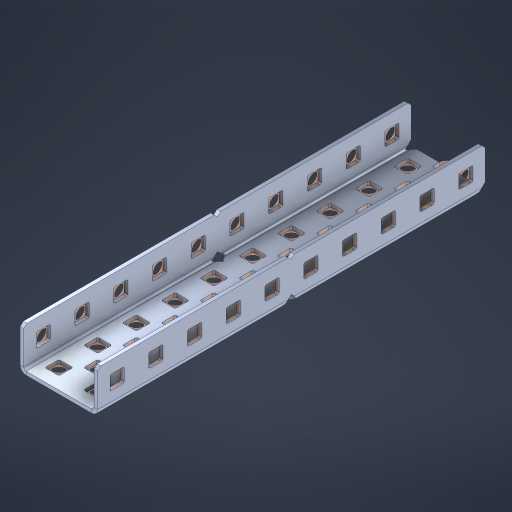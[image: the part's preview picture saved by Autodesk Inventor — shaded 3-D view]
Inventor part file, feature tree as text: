
AUTODESK INVENTOR PART (.ipt)
format: ipt  version: 2023 (Build 270158000, 158)  size: 927,744 bytes
history: native  units: in
note: dims shown in document units (in); Inventor stores cm internally (conversion verified against a paired STEP export)
features: other x57, extrude x48, sheet_metal_op x11, sketch x10, pattern_linear x2, mirror x1, chamfer x1
ambient origin geometry x8: Origin, YZ Plane, XZ Plane, XY Plane, X Axis, Y Axis, Z Axis, Center Point
bodies: Solid1 (feature_tree), Body (feature_tree)
feature tree (130):
  sheet_metal_op  "Flanges"
  other  "Flange Pattern Plane"
  other  "Flange Pattern Sketch"
  sheet_metal_op  "Flange Pattern"
  sheet_metal_op  "Body Pattern"
  pattern_linear  "Center Pattern"  Spacing1=0.0469in  [1 undecoded]
  other  "Arc Length"
  mirror  "Notch Mirror"
  pattern_linear  "Notch Pattern"  Spacing1=0.182in  [1 undecoded]
  chamfer  "End Chamfer"
  extrude  "Half Cut"  Depth=0.02in
  sketch  "Sketch1"  dims[d0=1.0in]
  other  "Plate1"
  sketch  "Sketch2"  dims[d1=5.0in]
  other  "Plate2"
  sheet_metal_op  "Bend1"
  sheet_metal_op  "Corner1"
  sketch  "Sketch3"  dims[d2=0.0469in]
  sketch  "Sketch7"  dims[d3=0.0469in]
  other  "Srf1"
  other  "Srf2"
  sketch  "Sketch8"  dims[d4=0.0234in]
  sketch  "Sketch9"  dims[d5=0.0938in]
  other  "Srf91"
  sheet_metal_op  "Body Pattern Sketch"
  other  "Srf92"
  sketch  "Sketch13"  dims[d6=0.0469in]
  sketch  "Sketch14"  dims[d7=0.5in d8=90.0deg d9=0.0312in]
  sketch  "Sketch15"  dims[d10=0.1875in]
  sketch  "Sketch16"  dims[d11=0.0469in d12=0.0469in d16=0.182in d17=0.02in d18=0.0469in d19=0.0in d20=0.25in d21=0.25in d38=3.937in d40=0.5in d41=0.7874in d43=1.0in d46=0.172in d47=1.0in d48=0.0in d49=0.182in d50=0.02in d51=0.25in d52=0.25in d53=0.0469in d54=0.0in d55=0.172in d56=1.0in d57=0.0in d58=0.25in d60=3.937in d62=0.5in d63=0.7874in d65=0.5in d85=0.1227in d86=0.1659in d88=0.04in d89=0.0469in d90=0.0in d91=0.04in d92=0.0491in d95=2.5in d96=0.04in d97=0.25in d98=45.0deg d99=0.25in d100=0.5in d101=0.0in d102=2.497in d106=0.182in d107=0.02in d108=0.5in d109=0.5in d110=0.0469in d111=0.0in d112=0.172in d113=0.5in d114=0.0in d117=0.5in d118=0.5in d119=0.5in]
  other  "Srf786"
  other  "Srf823"
  other  "Srf824"
  other  "Srf825"
  other  "Srf826"
  other  "Srf827"
  other  "Srf828"
  other  "Srf829"
  other  "Srf856"
  other  "Srf857"
  other  "Srf858"
  other  "Srf859"
  other  "Srf860"
  other  "Srf861"
  other  "Srf862"
  other  "Srf889"
  other  "Srf890"
  other  "Srf891"
  other  "Srf892"
  other  "Srf893"
  other  "Srf894"
  other  "Srf895"
  other  "Srf896"
  other  "Srf922"
  other  "Srf923"
  other  "Srf924"
  other  "Srf925"
  other  "Srf926"
  other  "Srf959"
  other  "Srf960"
  other  "Srf961"
  other  "Srf962"
  other  "Srf963"
  other  "Srf996"
  other  "Srf1143"
  other  "Srf1144"
  other  "Srf1145"
  other  "Srf1146"
  other  "Srf1147"
  other  "Srf1148"
  other  "Srf1199"
  other  "Srf1200"
  other  "Srf1201"
  other  "Srf1202"
  other  "Srf1203"
  other  "Srf1204"
  sheet_metal_op  "Flange Stamp"
  sheet_metal_op  "Flange Circle"
  sheet_metal_op  "Body Stamp"
  sheet_metal_op  "Body Circle"
  other  "Center Stamp"
  other  "Center Circle"
  sheet_metal_op  "Notch"
  extrude  "ExtrusionSrf2"  Depth=0.0469in
  extrude  "ExtrusionSrf92"  TaperAngle=0.0deg  [1 undecoded]
  extrude  "ExtrusionSrf823"  Depth=0.5in
  extrude  "ExtrusionSrf824"  Depth=0.5in
  extrude  "ExtrusionSrf825"  Depth=0.5in
  extrude  "ExtrusionSrf826"  Depth=0.5in
  extrude  "ExtrusionSrf827"  Depth=1.0in TaperAngle=0.0deg
  extrude  "ExtrusionSrf828"  Depth=0.5in
  extrude  "ExtrusionSrf829"  Depth=0.02in
  extrude  "ExtrusionSrf856"  Depth=0.5in
  extrude  "ExtrusionSrf857"  Depth=0.5in
  extrude  "ExtrusionSrf858"  Depth=0.0469in
  extrude  "ExtrusionSrf859"  TaperAngle=0.0deg  [1 undecoded]
  extrude  "ExtrusionSrf860"  Depth=0.5in
  extrude  "ExtrusionSrf861"  Depth=1.0in TaperAngle=0.0deg
  extrude  "ExtrusionSrf862"  Depth=0.5in
  extrude  "ExtrusionSrf889"  Depth=0.5in
  extrude  "ExtrusionSrf890"  Depth=0.5in
  extrude  "ExtrusionSrf891"  Depth=0.5in
  extrude  "ExtrusionSrf892"  Depth=0.5in
  extrude  "ExtrusionSrf893"  Depth=0.5in
  extrude  "ExtrusionSrf894"  Depth=0.0469in
  extrude  "ExtrusionSrf895"  TaperAngle=0.0deg  [1 undecoded]
  extrude  "ExtrusionSrf896"  Depth=0.5in
  extrude  "ExtrusionSrf922"  Depth=0.5in
  extrude  "ExtrusionSrf923"  Depth=2.5in
  extrude  "ExtrusionSrf924"  Depth=0.5in TaperAngle=45.0deg
  extrude  "ExtrusionSrf925"  Depth=0.5in
  extrude  "ExtrusionSrf926"  Depth=0.5in TaperAngle=0.0deg
  extrude  "ExtrusionSrf959"  Depth=0.5in
  extrude  "ExtrusionSrf960"  Depth=0.5in
  extrude  "ExtrusionSrf961"  Depth=0.02in
  extrude  "ExtrusionSrf962"  Depth=0.5in
  extrude  "ExtrusionSrf963"  Depth=0.5in
  extrude  "ExtrusionSrf996"  Depth=0.0469in
  extrude  "ExtrusionSrf1143"  TaperAngle=0.0deg  [1 undecoded]
  extrude  "ExtrusionSrf1144"  Depth=0.5in
  extrude  "ExtrusionSrf1145"  Depth=0.5in TaperAngle=0.0deg
  extrude  "ExtrusionSrf1146"  Depth=0.5in
  extrude  "ExtrusionSrf1147"  Depth=0.5in
  extrude  "ExtrusionSrf1148"  Depth=0.5in
  extrude  "ExtrusionSrf1199"  [1 undecoded]
  extrude  "ExtrusionSrf1200"  [1 undecoded]
  extrude  "ExtrusionSrf1201"  [1 undecoded]
  extrude  "ExtrusionSrf1202"  [1 undecoded]
  extrude  "ExtrusionSrf1203"  [1 undecoded]
  extrude  "ExtrusionSrf1204"  [1 undecoded]
note: 12 required parameter values undecoded (feature->parameter linkage not recoverable at this tier; creation-order binding heuristic only, values carry confidence <= 0.55)
